# Revit family: Toilet_Seat-Elongated_Closed_Front-Cleansing-KOHLER-Purewash-K-98804_1
name_source: partatom
category: Plumbing Fixtures
revit_build: Autodesk Revit 2017 (Build: 20160225_1515(x64)
units: mm (PartAtom-declared; Revit-internal decimal feet)

## family parameters
Cut with Voids When Loaded = No
Host = Face
OmniClass Number = 23.31.19.19.19
OmniClass Title = Water Closet Tanks
Part Type = Normal
Room Calculation Point = No
Round Connector Dimension = Use Diameter
Shared = No

## types (4) — shared parameters
ADA Compliant = No
Assembly Code = D2010100
CW Connection = Yes
Cold Water Inlet = Cold Water Inlet
Date Modified = 12/28/2021
Default Elevation = 15"
Flow Rate = 0 GPM
HW Connection = No
Height = 3 1/16"
Hot Water Inlet = Hot Water Inlet
Length = 19 15/16"
Manufacturer = KOHLER Co.
Master Format 2014 = 22 42 13.13
Master Format 2014 Name = Toilet, Bath, and Laundry Accessories
Material = Plastic
Pressure = 0.00 psi
Product Documentation Link = https://www.us.kohler.com
Product Name = Purewash
Product Page URL = http://www.us.kohler.com
URL = https://www.us.kohler.com
Vent Connection = No
Waste Connection = No
WaterSense Certified = No
Width = 14 1/2"

## per-type parameters (varying)
| type | Chrome Handle | Description | Finish | Model | Plastic Handle | Type |
| 0-White | No | Elongated Manual Bidet Seat | Kohler-Plastic-0-White | K-98804-0 | Yes | 1 |
| Polished Chrome Handle, 0-White | Yes | Elongated Manual Bidet Toilet Seat With Polished Chrome Handle | Kohler-Plastic-0-White | K-98804-CP-0 | No | 3 |
| 58-Thunder Grey | No | Elongated Manual Bidet Seat | Kohler-Plastic-58-Thunder_Grey | K-98804-58 | Yes | 2 |
| Polished Chrome Handle, 58-Thunder Grey | Yes | Elongated Manual Bidet Toilet Seat With Polished Chrome Handle | Kohler-Plastic-58-Thunder_Grey | K-98804-CP-58 | No | 4 |

## geometry (parser evidence)
native form markers: Sweep x5
no freeform markers — native parametric forms only
